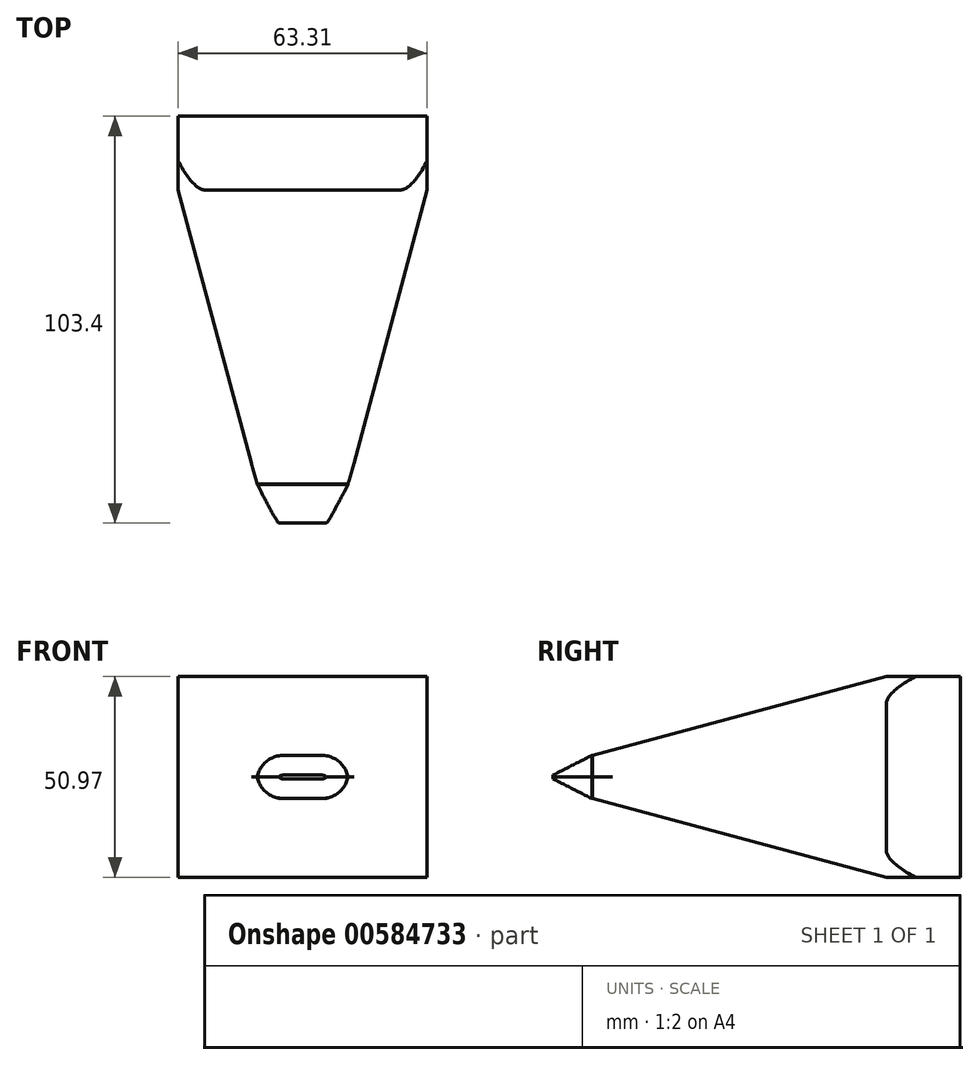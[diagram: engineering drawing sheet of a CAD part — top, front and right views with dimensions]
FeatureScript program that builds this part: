
annotation { "Feature Type Name" : "Feature", "Feature Type Description" : "" }
export const myFeature = defineFeature(function(context is Context, id is Id, definition is map)
    precondition{}
    {
        {
            var Q0;
            Q0=qCreatedBy(makeId("Front.planeOp"),FACE);
            var sketch = newSketch(context, id + "F0", { "sketchPlane" : qUnion([Q0])});
            skLineSegment(sketch, "E0.bottom", {"start": v(0, 23.73) * mm, "end": v(63.31, 23.73) * mm});
            skLineSegment(sketch, "E0.top", {"start": v(0, -27.24) * mm, "end": v(63.31, -27.24) * mm});
            skLineSegment(sketch, "E0.left", {"start": v(63.31, 23.73) * mm, "end": v(63.31, -27.24) * mm});
            skLineSegment(sketch, "E0.right", {"start": v(0, 23.73) * mm, "end": v(0, -27.24) * mm});
            skSolve(sketch);
        }
        {
            var Q0;
            Q0=makeQuery(id+"F0.imprint","IMPRINT",FACE,{"disambiguationData":[TD([[makeQuery(id+"F0.imprint","IMPRINT",EDGE,{"derivedFrom":sQuery(id+"F0.wireOp",EDGE,"E0.bottom")}),-1.0]])]});
            extrude(context, id + "F1", {"entities" : qUnion([Q0]), "depth" : 93.4 * mm, "offsetDistance" : 25 * mm});
        }
        {
            var Q0;
            Q0=makeQuery(id+"F1.opExtrude","CAP_FACE",FACE,{"disambiguationData":[OSD([sQuery(id+"F0.wireOp",EDGE,"E0.bottom"),sQuery(id+"F0.wireOp",EDGE,"E0.top"),sQuery(id+"F0.wireOp",EDGE,"E0.left"),sQuery(id+"F0.wireOp",EDGE,"E0.right")])],"isStart":false});
            chamfer(context, id + "F2", {"entities" : qUnion([Q0]), "chamferType" : ChamferType.OFFSET_ANGLE, "width" : 20 * mm, "oppositeDirection" : true, "angle" : 75 * degree, "tangentPropagation" : true});
        }
        {
            var Q0;
            Q0=makeQuery(id+"F2.opChamfer","BLEND_EDGE",EDGE,{"blendedFrom":[makeQuery(id+"F1.opExtrude","CAP_EDGE",EDGE,{"disambiguationData":[OSD([sQuery(id+"F0.wireOp",EDGE,"E0.bottom")])],"isStart":false}),makeQuery(id+"F1.opExtrude","CAP_EDGE",EDGE,{"disambiguationData":[OSD([sQuery(id+"F0.wireOp",EDGE,"E0.left")])],"isStart":false})],"blendedInto":[]});
            var Q1;
            Q1=makeQuery(id+"F2.opChamfer","BLEND_EDGE",EDGE,{"blendedFrom":[makeQuery(id+"F1.opExtrude","CAP_EDGE",EDGE,{"disambiguationData":[OSD([sQuery(id+"F0.wireOp",EDGE,"E0.bottom")])],"isStart":false}),makeQuery(id+"F1.opExtrude","CAP_EDGE",EDGE,{"disambiguationData":[OSD([sQuery(id+"F0.wireOp",EDGE,"E0.right")])],"isStart":false})],"blendedInto":[]});
            var Q2;
            Q2=makeQuery(id+"F2.opChamfer","BLEND_EDGE",EDGE,{"blendedFrom":[makeQuery(id+"F1.opExtrude","CAP_EDGE",EDGE,{"disambiguationData":[OSD([sQuery(id+"F0.wireOp",EDGE,"E0.top")])],"isStart":false}),makeQuery(id+"F1.opExtrude","CAP_EDGE",EDGE,{"disambiguationData":[OSD([sQuery(id+"F0.wireOp",EDGE,"E0.left")])],"isStart":false})],"blendedInto":[]});
            var Q3;
            Q3=makeQuery(id+"F2.opChamfer","BLEND_EDGE",EDGE,{"blendedFrom":[makeQuery(id+"F1.opExtrude","CAP_EDGE",EDGE,{"disambiguationData":[OSD([sQuery(id+"F0.wireOp",EDGE,"E0.top")])],"isStart":false}),makeQuery(id+"F1.opExtrude","CAP_EDGE",EDGE,{"disambiguationData":[OSD([sQuery(id+"F0.wireOp",EDGE,"E0.right")])],"isStart":false})],"blendedInto":[]});
            fillet(context, id + "F3", {"entities" : qUnion([Q0, Q1, Q2, Q3]), "radius" : 7.1 * mm, "tangentPropagation" : true, "allowEdgeOverflow" : false});
        }
        {
            var Q0;
            Q0=makeQuery(id+"F1.opExtrude","SWEPT_BODY",BODY,{"disambiguationData":[OSD([sQuery(id+"F0.wireOp",EDGE,"E0.bottom"),sQuery(id+"F0.wireOp",EDGE,"E0.top"),sQuery(id+"F0.wireOp",EDGE,"E0.left"),sQuery(id+"F0.wireOp",EDGE,"E0.right")])]});
            transform(context, id + "F4", {"entities" : qUnion([Q0]), "transformType" : TransformType.TRANSLATION_3D, "dx" : 0 * mm, "dy" : 0 * mm, "dz" : 0 * mm, "makeCopy" : true});
        }
        {
            var Q0;
            Q0=makeQuery(id+"F4.opPattern","COPY",FACE,{"derivedFrom":makeQuery(id+"F1.opExtrude","CAP_FACE",FACE,{"disambiguationData":[OSD([sQuery(id+"F0.wireOp",EDGE,"E0.bottom"),sQuery(id+"F0.wireOp",EDGE,"E0.top"),sQuery(id+"F0.wireOp",EDGE,"E0.left"),sQuery(id+"F0.wireOp",EDGE,"E0.right")])],"isStart":false}),"instanceName":"1"});
            extrude(context, id + "F5", {"entities" : qUnion([Q0]), "operationType" : NewBodyOperationType.ADD, "depth" : 10 * mm, "offsetDistance" : 25 * mm});
        }
        {
            var Q0;
            Q0=makeQuery(id+"F5.opExtrude","CAP_FACE",FACE,{"disambiguationData":[OSD([sQuery(id+"F0.wireOp",EDGE,"E0.bottom"),sQuery(id+"F0.wireOp",EDGE,"E0.top"),sQuery(id+"F0.wireOp",EDGE,"E0.left"),sQuery(id+"F0.wireOp",EDGE,"E0.right")])],"isStart":false});
            chamfer(context, id + "F6", {"entities" : qUnion([Q0]), "chamferType" : ChamferType.OFFSET_ANGLE, "width" : 5 * mm, "oppositeDirection" : false, "angle" : 63 * degree, "tangentPropagation" : true});
        }
    });
